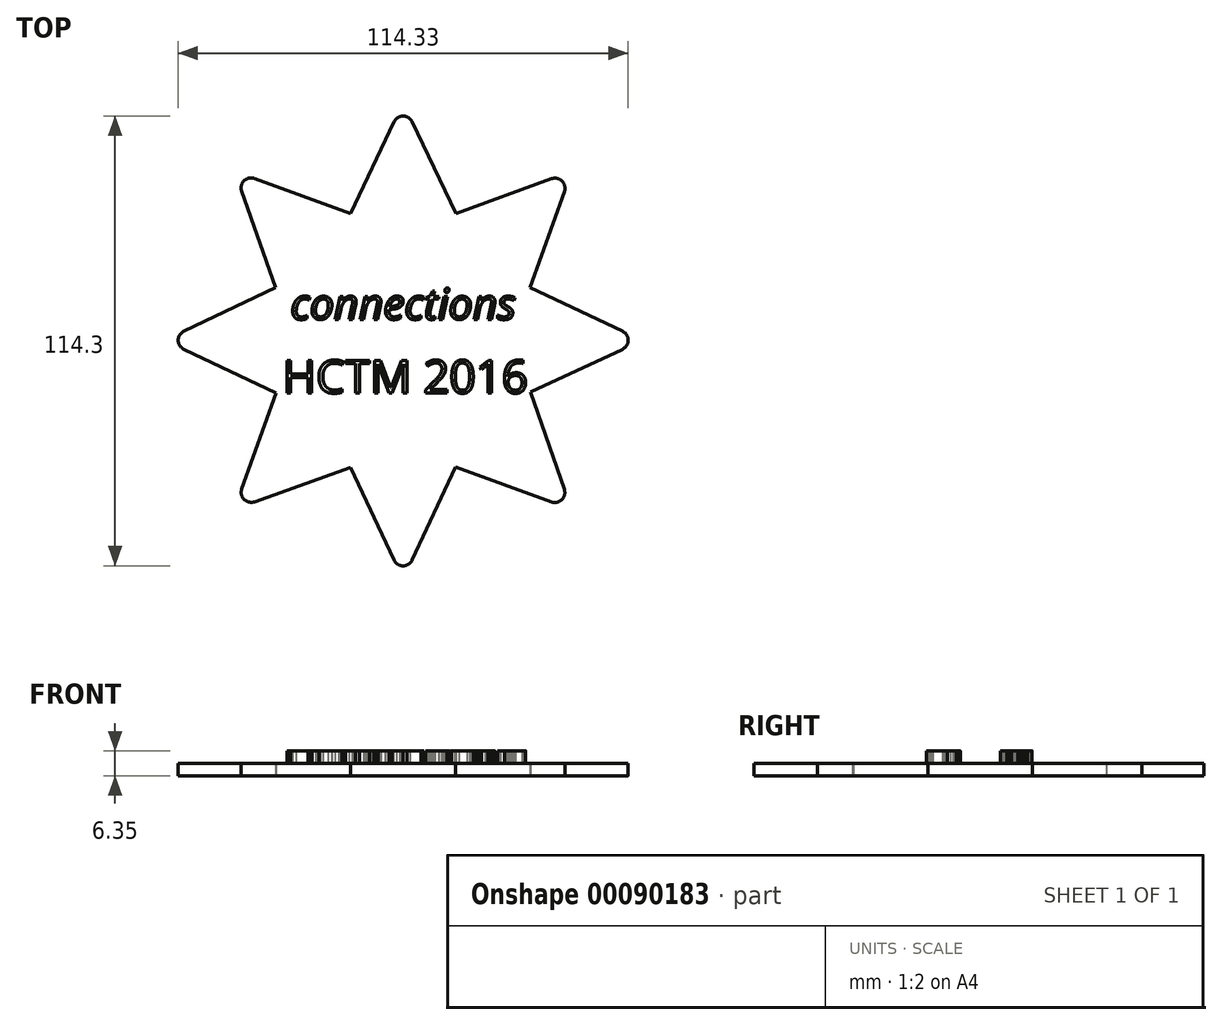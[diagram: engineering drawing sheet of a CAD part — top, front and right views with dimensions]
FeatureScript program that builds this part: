
annotation { "Feature Type Name" : "Feature", "Feature Type Description" : "" }
export const myFeature = defineFeature(function(context is Context, id is Id, definition is map)
    precondition{}
    {
        {
            var Q0;
            Q0=qCreatedBy(makeId("Top.planeOp"),FACE);
            var sketch = newSketch(context, id + "F0", { "sketchPlane" : qUnion([Q0])});
            skLineSegment(sketch, "E0", {"start": v(-41.74, 95.33) * mm, "end": v(-28.36, 67.1) * mm});
            skLineSegment(sketch, "E1", {"start": v(-28.36, 67.1) * mm, "end": v(1.06, 77.84) * mm});
            skLineSegment(sketch, "E2", {"start": v(1.06, 77.84) * mm, "end": v(-9.5, 48.36) * mm});
            skLineSegment(sketch, "E3", {"start": v(-9.5, 48.36) * mm, "end": v(18.87, 34.94) * mm});
            skLineSegment(sketch, "E4", {"start": v(18.87, 34.94) * mm, "end": v(-9.36, 21.8) * mm});
            skLineSegment(sketch, "E5", {"start": v(-9.36, 21.8) * mm, "end": v(0.94, -7.97) * mm});
            skLineSegment(sketch, "E6", {"start": v(0.94, -7.97) * mm, "end": v(-28.45, 2.8) * mm});
            skLineSegment(sketch, "E7", {"start": v(-28.45, 2.8) * mm, "end": v(-41.74, -25.84) * mm});
            skLineSegment(sketch, "E8", {"start": v(-41.74, -25.84) * mm, "end": v(-55.07, 2.57) * mm});
            skLineSegment(sketch, "E9", {"start": v(-55.07, 2.57) * mm, "end": v(-84.55, -7.86) * mm});
            skLineSegment(sketch, "E10", {"start": v(-84.55, -7.86) * mm, "end": v(-74, 21.56) * mm});
            skLineSegment(sketch, "E11", {"start": v(-74, 21.56) * mm, "end": v(-102.3, 34.94) * mm});
            skLineSegment(sketch, "E12", {"start": v(-102.3, 34.94) * mm, "end": v(-74.11, 48.32) * mm});
            skLineSegment(sketch, "E13", {"start": v(-74.11, 48.32) * mm, "end": v(-84.55, 77.92) * mm});
            skLineSegment(sketch, "E14", {"start": v(-84.55, 77.92) * mm, "end": v(-55.07, 67.13) * mm});
            skLineSegment(sketch, "E15", {"start": v(-55.07, 67.13) * mm, "end": v(-41.74, 95.33) * mm});
            skSolve(sketch);
        }
        {
            var Q0;
            Q0=makeQuery(id+"F0.imprint","IMPRINT",FACE,{"disambiguationData":[TD([[makeQuery(id+"F0.imprint","IMPRINT",EDGE,{"derivedFrom":sQuery(id+"F0.wireOp",EDGE,"E0")}),-1.0]])]});
            var Q1;
            Q1=sQuery(id+"F0.wireOp",EDGE,"E0");
            var Q2;
            Q2=sQuery(id+"F0.wireOp",EDGE,"E1");
            var Q3;
            Q3=sQuery(id+"F0.wireOp",EDGE,"E2");
            var Q4;
            Q4=sQuery(id+"F0.wireOp",EDGE,"E3");
            var Q5;
            Q5=sQuery(id+"F0.wireOp",EDGE,"E4");
            var Q6;
            Q6=sQuery(id+"F0.wireOp",EDGE,"E5");
            var Q7;
            Q7=sQuery(id+"F0.wireOp",EDGE,"E6");
            var Q8;
            Q8=sQuery(id+"F0.wireOp",EDGE,"E7");
            var Q9;
            Q9=sQuery(id+"F0.wireOp",EDGE,"E8");
            var Q10;
            Q10=sQuery(id+"F0.wireOp",EDGE,"E9");
            var Q11;
            Q11=sQuery(id+"F0.wireOp",EDGE,"E10");
            var Q12;
            Q12=sQuery(id+"F0.wireOp",EDGE,"E11");
            var Q13;
            Q13=sQuery(id+"F0.wireOp",EDGE,"E12");
            var Q14;
            Q14=sQuery(id+"F0.wireOp",EDGE,"E13");
            var Q15;
            Q15=sQuery(id+"F0.wireOp",EDGE,"E14");
            var Q16;
            Q16=sQuery(id+"F0.wireOp",EDGE,"E15");
            extrude(context, id + "F1", {"entities" : qUnion([Q0]), "surfaceEntities" : qUnion([Q1, Q2, Q3, Q4, Q5, Q6, Q7, Q8, Q9, Q10, Q11, Q12, Q13, Q14, Q15, Q16]), "depth" : 3.17 * mm});
        }
        {
            var Q0;
            Q0=makeQuery(id+"F1.opExtrude","CAP_FACE",FACE,{"disambiguationData":[OSD([sQuery(id+"F0.wireOp",EDGE,"E0"),sQuery(id+"F0.wireOp",EDGE,"E1"),sQuery(id+"F0.wireOp",EDGE,"E2"),sQuery(id+"F0.wireOp",EDGE,"E3"),sQuery(id+"F0.wireOp",EDGE,"E4"),sQuery(id+"F0.wireOp",EDGE,"E5"),sQuery(id+"F0.wireOp",EDGE,"E6"),sQuery(id+"F0.wireOp",EDGE,"E7"),sQuery(id+"F0.wireOp",EDGE,"E8"),sQuery(id+"F0.wireOp",EDGE,"E9"),sQuery(id+"F0.wireOp",EDGE,"E10"),sQuery(id+"F0.wireOp",EDGE,"E11"),sQuery(id+"F0.wireOp",EDGE,"E12"),sQuery(id+"F0.wireOp",EDGE,"E13"),sQuery(id+"F0.wireOp",EDGE,"E14"),sQuery(id+"F0.wireOp",EDGE,"E15")])],"isStart":false});
            var sketch = newSketch(context, id + "F2", { "sketchPlane" : qUnion([Q0])});
            skText(sketch, "E16", { "text": "connections", "fontName": "OpenSans-Italic.ttf"});
            skText(sketch, "E17", { "text": "HCTM 2016", "fontName": "OpenSans-Regular.ttf"});
            const initialGuessF2  = {"E16": [-0.07033, 0.04026, 1, 0, 0.00784], "E17": [-0.07243, 0.02156, 1, 0, 0.00836]};
            skSetInitialGuess(sketch, initialGuessF2);
            skSolve(sketch);
        }
        {
            var Q0;
            Q0 = qSketchRegion(id + "F2", true);
            extrude(context, id + "F3", {"entities" : qUnion([Q0]), "operationType" : NewBodyOperationType.ADD, "depth" : 3.17 * mm});
        }
        {
            var Q0;
            Q0=makeQuery(id+"F1.opExtrude","SWEPT_EDGE",EDGE,{"disambiguationData":[OSD([sQuery(id+"F0.wireOp",EDGE,"E11"),sQuery(id+"F0.wireOp",EDGE,"E12")])]});
            var Q1;
            Q1=makeQuery(id+"F1.opExtrude","SWEPT_EDGE",EDGE,{"disambiguationData":[OSD([sQuery(id+"F0.wireOp",EDGE,"E9"),sQuery(id+"F0.wireOp",EDGE,"E10")])]});
            var Q2;
            Q2=makeQuery(id+"F1.opExtrude","SWEPT_EDGE",EDGE,{"disambiguationData":[OSD([sQuery(id+"F0.wireOp",EDGE,"E7"),sQuery(id+"F0.wireOp",EDGE,"E8")])]});
            var Q3;
            Q3=makeQuery(id+"F1.opExtrude","SWEPT_EDGE",EDGE,{"disambiguationData":[OSD([sQuery(id+"F0.wireOp",EDGE,"E5"),sQuery(id+"F0.wireOp",EDGE,"E6")])]});
            var Q4;
            Q4=makeQuery(id+"F1.opExtrude","SWEPT_EDGE",EDGE,{"disambiguationData":[OSD([sQuery(id+"F0.wireOp",EDGE,"E3"),sQuery(id+"F0.wireOp",EDGE,"E4")])]});
            var Q5;
            Q5=makeQuery(id+"F1.opExtrude","SWEPT_EDGE",EDGE,{"disambiguationData":[OSD([sQuery(id+"F0.wireOp",EDGE,"E1"),sQuery(id+"F0.wireOp",EDGE,"E2")])]});
            var Q6;
            Q6=makeQuery(id+"F1.opExtrude","SWEPT_EDGE",EDGE,{"disambiguationData":[OSD([sQuery(id+"F0.wireOp",EDGE,"E0"),sQuery(id+"F0.wireOp",EDGE,"E15")])]});
            var Q7;
            Q7=makeQuery(id+"F1.opExtrude","SWEPT_EDGE",EDGE,{"disambiguationData":[OSD([sQuery(id+"F0.wireOp",EDGE,"E13"),sQuery(id+"F0.wireOp",EDGE,"E14")])]});
            fillet(context, id + "F4", {"entities" : qUnion([Q0, Q1, Q2, Q3, Q4, Q5, Q6, Q7]), "radius" : 2.54 * mm, "tangentPropagation" : true, "allowEdgeOverflow" : false});
        }
    });
